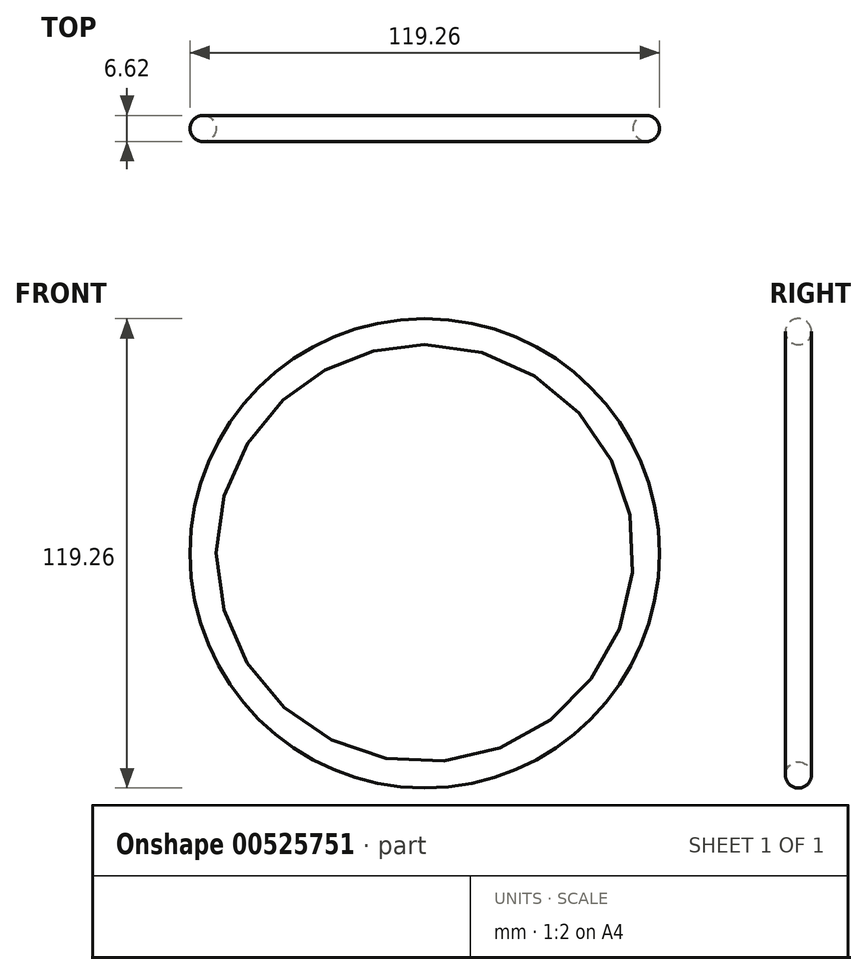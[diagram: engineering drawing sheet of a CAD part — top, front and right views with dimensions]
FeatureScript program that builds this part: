
annotation { "Feature Type Name" : "Feature", "Feature Type Description" : "" }
export const myFeature = defineFeature(function(context is Context, id is Id, definition is map)
    precondition{}
    {
        {
            var Q0;
            Q0=qCreatedBy(makeId("Top.planeOp"),FACE);
            var sketch = newSketch(context, id + "F0", { "sketchPlane" : qUnion([Q0])});
            skCircle(sketch, "E0", {"center": v(56.32, 0) * mm, "radius": 3.31 * mm});
            skLineSegment(sketch, "E1", {"start": v(0, 75.58) * mm, "end": v(0, -74.1) * mm});
            skSolve(sketch);
        }
        {
            var Q0;
            Q0 = qSketchRegion(id + "F0", true);
            var Q1;
            Q1=sQuery(id+"F0.wireOp",EDGE,"E1");
            revolve(context, id + "F1", {"entities" : qUnion([Q0]), "axis" : qUnion([Q1]), "revolveType" : RevolveType.FULL});
        }
    });
